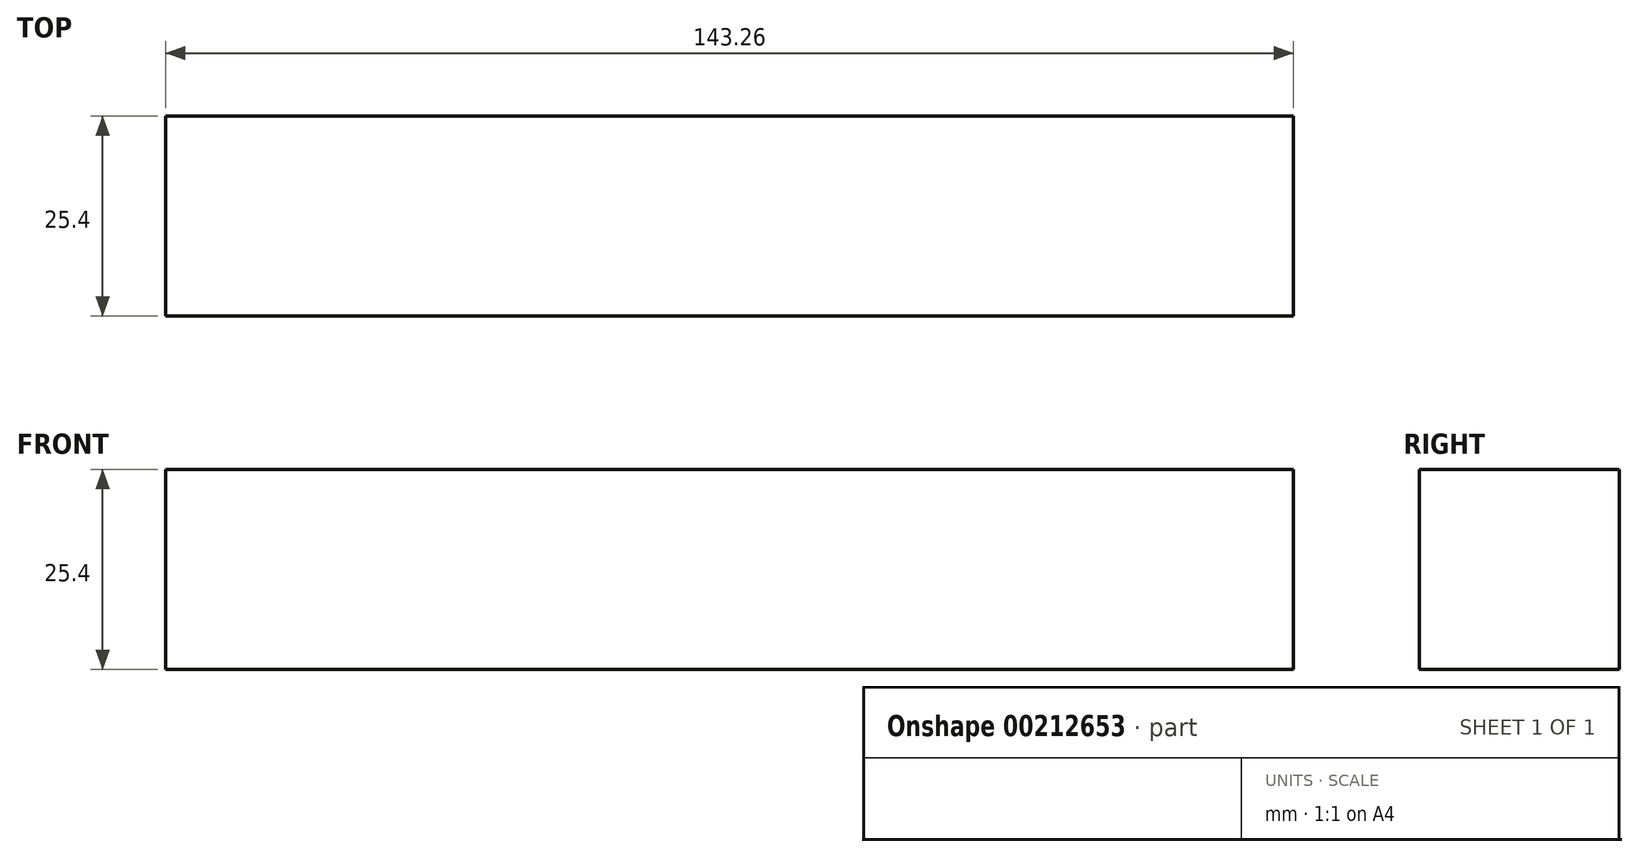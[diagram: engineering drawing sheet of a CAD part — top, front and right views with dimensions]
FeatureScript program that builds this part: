
annotation { "Feature Type Name" : "Feature", "Feature Type Description" : "" }
export const myFeature = defineFeature(function(context is Context, id is Id, definition is map)
    precondition{}
    {
        {
            var Q0;
            Q0=qCreatedBy(makeId("Right.planeOp"),FACE);
            var sketch = newSketch(context, id + "F0", { "sketchPlane" : qUnion([Q0])});
            skLineSegment(sketch, "E0.bottom", {"start": v(12.7, 12.7) * mm, "end": v(-12.7, 12.7) * mm});
            skLineSegment(sketch, "E0.top", {"start": v(12.7, -12.7) * mm, "end": v(-12.7, -12.7) * mm});
            skLineSegment(sketch, "E0.left", {"start": v(12.7, 12.7) * mm, "end": v(12.7, -12.7) * mm});
            skLineSegment(sketch, "E0.right", {"start": v(-12.7, 12.7) * mm, "end": v(-12.7, -12.7) * mm});
            skPoint(sketch, "E0.middle", {"position": v(0, 0) * mm});
            skSolve(sketch);
        }
        {
            var Q0;
            Q0 = qSketchRegion(id + "F0", true);
            extrude(context, id + "F1", {"entities" : qUnion([Q0]), "depth" : 143.26 * mm});
        }
    });
